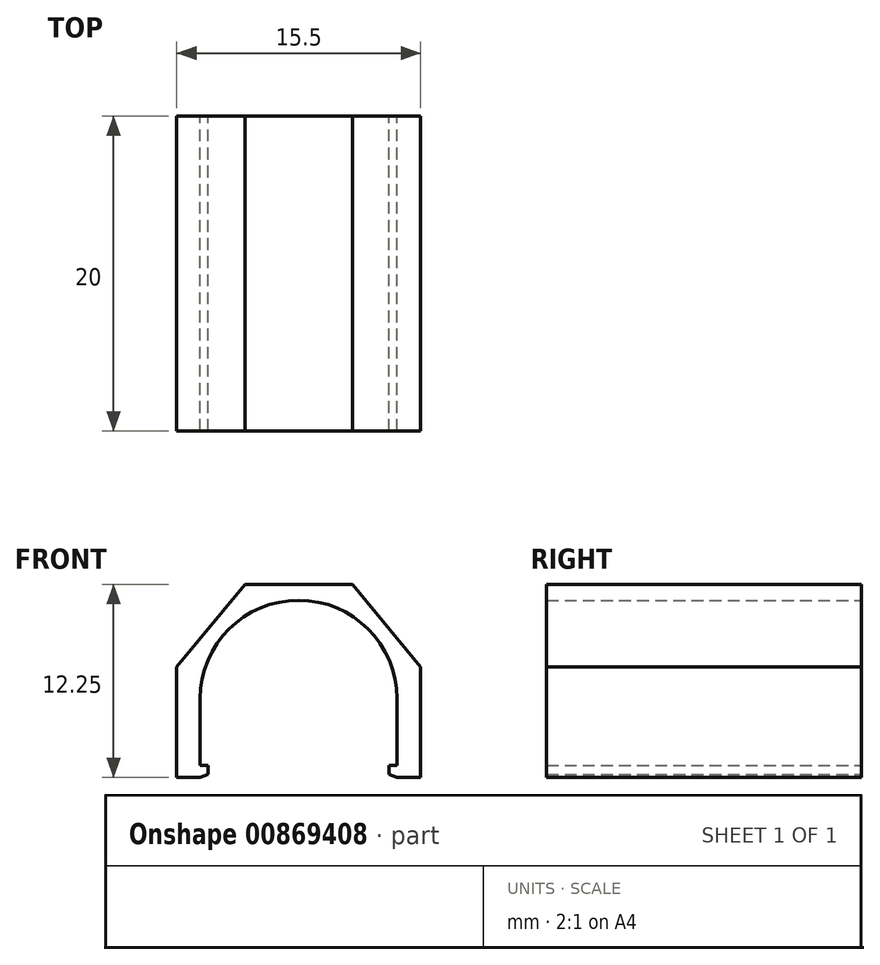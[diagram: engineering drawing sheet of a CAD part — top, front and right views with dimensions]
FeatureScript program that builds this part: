
annotation { "Feature Type Name" : "Feature", "Feature Type Description" : "" }
export const myFeature = defineFeature(function(context is Context, id is Id, definition is map)
    precondition{}
    {
        {
            var Q0;
            Q0=qCreatedBy(makeId("Front.planeOp"),FACE);
            var sketch = newSketch(context, id + "F0", { "sketchPlane" : qUnion([Q0])});
            skLineSegment(sketch, "E0", {"start": v(0, 0) * mm, "end": v(0, 7) * mm});
            skLineSegment(sketch, "E1", {"start": v(15.5, 7) * mm, "end": v(15.5, 0) * mm});
            skLineSegment(sketch, "E2", {"start": v(15.5, 0) * mm, "end": v(14, 0) * mm});
            skLineSegment(sketch, "E3", {"start": v(14, 0.75) * mm, "end": v(14, 5) * mm});
            skArc(sketch, "E4", {"start": v(14, 5) * mm, "mid": v(7.75, 11.25) * mm, "end": v(1.5, 5) * mm});
            skLineSegment(sketch, "E5", {"start": v(0, 0) * mm, "end": v(1.5, 0) * mm});
            skLineSegment(sketch, "E6", {"start": v(1.5, 0.75) * mm, "end": v(1.5, 5) * mm});
            skLineSegment(sketch, "E7", {"start": v(2, 0.2) * mm, "end": v(2, 0.75) * mm});
            skLineSegment(sketch, "E8", {"start": v(2, 0.75) * mm, "end": v(1.5, 0.75) * mm});
            skLineSegment(sketch, "E9", {"start": v(7.75, 5) * mm, "end": v(7.75, 0) * mm, "construction": true});
            skLineSegment(sketch, "E10.MirrorCS", {"start": v(13.5, 0.75) * mm, "end": v(14, 0.75) * mm});
            skLineSegment(sketch, "E11.MirrorCS", {"start": v(13.5, 0.2) * mm, "end": v(13.5, 0.75) * mm});
            skLineSegment(sketch, "E12", {"start": v(0, 7) * mm, "end": v(4.33, 12.25) * mm});
            skLineSegment(sketch, "E13", {"start": v(4.33, 12.25) * mm, "end": v(7.75, 12.25) * mm});
            skPoint(sketch, "E13.endSnap0", {"position": v(7.75, 11.25) * mm});
            skLineSegment(sketch, "E14.MirrorCS", {"start": v(11.17, 12.25) * mm, "end": v(7.75, 12.25) * mm});
            skLineSegment(sketch, "E15.MirrorCS", {"start": v(15.5, 7) * mm, "end": v(11.17, 12.25) * mm});
            skLineSegment(sketch, "E16", {"start": v(1.5, 0) * mm, "end": v(2, 0.2) * mm});
            skLineSegment(sketch, "E17", {"start": v(14, 0) * mm, "end": v(13.5, 0.2) * mm});
            skPoint(sketch, "E18.MirrorCS.end.orphan", {"position": v(14, 0) * mm});
            skSolve(sketch);
        }
        {
            var Q0;
            Q0=makeQuery(id+"F0.imprint","IMPRINT",FACE,{"disambiguationData":[TD([[makeQuery(id+"F0.imprint","IMPRINT",EDGE,{"derivedFrom":sQuery(id+"F0.wireOp",EDGE,"E0")}),-1.0]])]});
            extrude(context, id + "F1", {"entities" : qUnion([Q0]), "depth" : 20 * mm, "offsetDistance" : 25 * mm});
        }
    });
